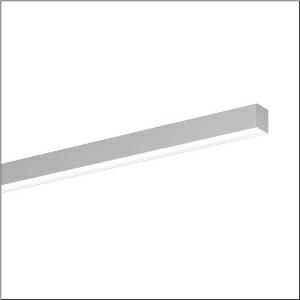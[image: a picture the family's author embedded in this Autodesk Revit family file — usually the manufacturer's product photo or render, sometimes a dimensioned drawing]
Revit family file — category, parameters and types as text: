
# Revit family: silica_r__21_51mx23tbt5s_3fb0
name_source: partatom
category: Lighting Fixtures
units: mm (PartAtom-declared; Revit-internal decimal feet)

## family parameters
Cut with Voids When Loaded = No
Host = Face
Light Source = No
Part Type = Normal
Room Calculation Point = No
Round Connector Dimension = Use Diameter
Shared = No

## types (1)
- --- (1 x LED, 4030 lm, 40.5 W, 6500K)
    Apparent Load = 41 VA
    CIE Flux Codes = 78 96 99 100 100
    Color Rendering = 80
    Color Temperature = 6500K
    Default Elevation = 1800 mm
    Description = Silica® 21, office luminaire, primary optical cover: prismatic diffuser, of PMMA, CAT 2 (L<= 3000cd/m²), light emission: direct distribution, primary light characteristic: symmetric, installation type: surface-mounted, LED, rated luminous flux: 4.030lm, luminous efficacy: 95lm/W, light colour: 8tw, colour temperature: 2700..6500K, control gear: DALI DT8, with terminal, 3+2-pole, max. 2.5mm², mains connection: 220..240V, AC, 50/60Hz, rated input power: 42.6W, luminaire housing, of aluminium, metallic grey (RAL 9006), length: 1.504mm, width: 53mm, height: 53mm, protection rating (complete): IP20, insulation class (complete): insulation class I (protective earthing), certification: CE, permissible operating ambient temperature: 0..+35°C, standard: EN 50419, packaging unit: 1 piece
    Height = 53 mm
    Lamp = 1 x LED
    Lamp Light Flux = 4030 lm
    Lamp Power = 40.5 W
    Lamp count = 1
    Length = 1504 mm
    Luminous efficacy = 100 lm/W
    Manufacturer = Siteco
    ModVariant = No
    Model = 51MX23TBT5S
    Mounting Place = Ceiling
    Mounting Type = Surface mounted
    Number of Poles = 1
    OnlyDefault = Yes
    Power Factor = 1
    Product Name = Silica® 21
    Product group = office luminaire | ceiling mounted
    ProductGroupID = 302
    Protection Class = Protection class I
    Protection Degree = IP 20
    RLX_Detail_Level = 1
    RLX_Emergency_Light_Flux = 0 lm
    RLX_Emergency_Type = 0
    RLX_Emergency_Type_DB = No
    RlxData = <blob elided: 17989 chars, md5=b6cffd9f>
    Socket = socket
    Standby Power = 0 W
    System Light Flux = 4030 lm
    System Power = 41 W
    Type Comments = individual setting
    Type Image = l_1335933.jpg
    URL = http://relux.com
    VarID = @adj_139794
    Voltage = 0 V
    Weight = 0.00 kg
    Width = 53 mm

## geometry (parser evidence)
native form markers: Blend x4, Sweep x10
no freeform markers — native parametric forms only
